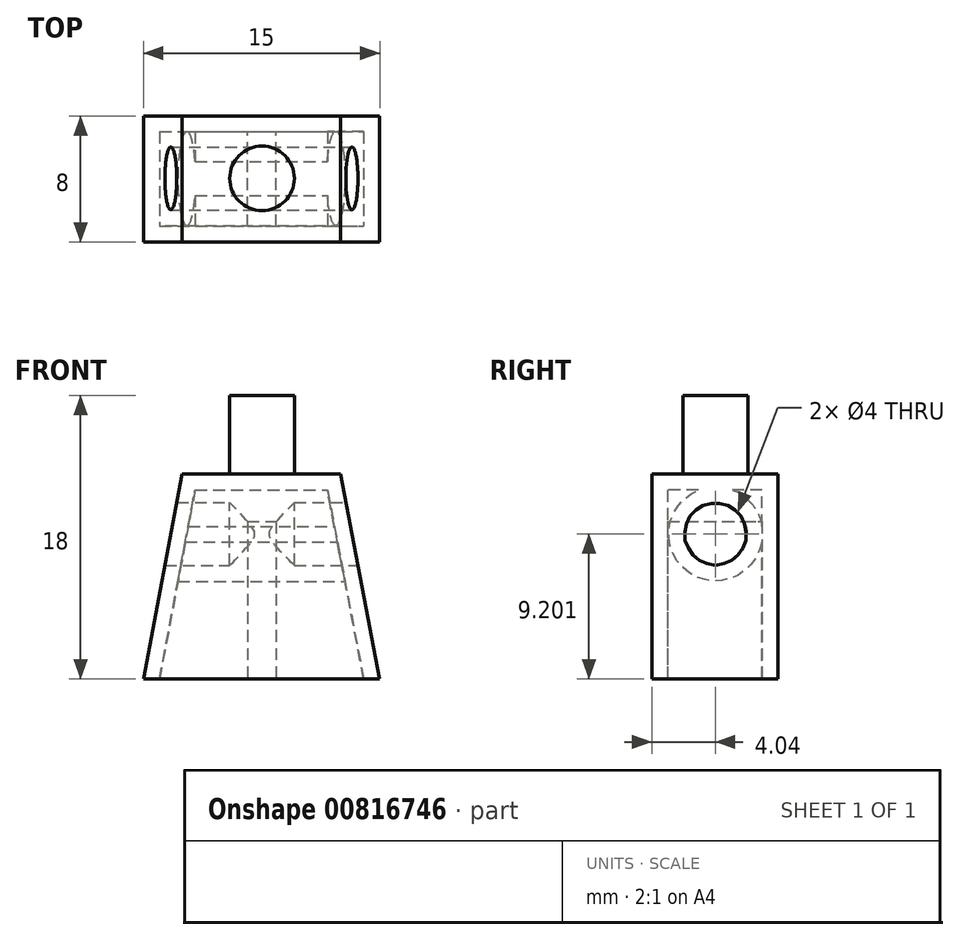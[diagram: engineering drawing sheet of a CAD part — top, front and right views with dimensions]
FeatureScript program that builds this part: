
annotation { "Feature Type Name" : "Feature", "Feature Type Description" : "" }
export const myFeature = defineFeature(function(context is Context, id is Id, definition is map)
    precondition{}
    {
        {
            var Q0;
            Q0=qCreatedBy(makeId("Top.planeOp"),FACE);
            var sketch = newSketch(context, id + "F0", { "sketchPlane" : qUnion([Q0])});
            skLineSegment(sketch, "E0.bottom", {"start": v(-7.52, 3.96) * mm, "end": v(7.48, 3.96) * mm});
            skLineSegment(sketch, "E0.top", {"start": v(-7.52, -4.04) * mm, "end": v(7.48, -4.04) * mm});
            skLineSegment(sketch, "E0.left", {"start": v(-7.52, 3.96) * mm, "end": v(-7.52, -4.04) * mm});
            skLineSegment(sketch, "E0.right", {"start": v(7.48, 3.96) * mm, "end": v(7.48, -4.04) * mm});
            skSolve(sketch);
        }
        {
            var Q0;
            Q0 = qSketchRegion(id + "F0", true);
            extrude(context, id + "F1", {"entities" : qUnion([Q0]), "depth" : 13 * mm, "offsetDistance" : 25 * mm});
        }
        {
            var Q0;
            Q0=makeQuery(id+"F1.opExtrude","CAP_FACE",FACE,{"disambiguationData":[OSD([sQuery(id+"F0.wireOp",EDGE,"E0.bottom"),sQuery(id+"F0.wireOp",EDGE,"E0.top"),sQuery(id+"F0.wireOp",EDGE,"E0.left"),sQuery(id+"F0.wireOp",EDGE,"E0.right")])],"isStart":false});
            var sketch = newSketch(context, id + "F2", { "sketchPlane" : qUnion([Q0])});
            skLineSegment(sketch, "E1.bottom", {"start": v(-5.04, 3.96) * mm, "end": v(4.96, 3.96) * mm});
            skLineSegment(sketch, "E1.top", {"start": v(-5.04, -4.04) * mm, "end": v(4.96, -4.04) * mm});
            skLineSegment(sketch, "E1.left", {"start": v(-5.04, 3.96) * mm, "end": v(-5.04, -4.04) * mm});
            skLineSegment(sketch, "E1.right", {"start": v(4.96, 3.96) * mm, "end": v(4.96, -4.04) * mm});
            skSolve(sketch);
        }
        {
            var Q0;
            Q0=makeQuery(id+"F1.opExtrude","SWEPT_FACE",FACE,{"disambiguationData":[OSD([sQuery(id+"F0.wireOp",EDGE,"E0.top")])]});
            var sketch = newSketch(context, id + "F3", { "sketchPlane" : qUnion([Q0])});
            skLineSegment(sketch, "E2", {"start": v(-5.08, 13) * mm, "end": v(-7.52, 0) * mm});
            skLineSegment(sketch, "E3", {"start": v(-7.52, 0) * mm, "end": v(-7.52, 13) * mm});
            skLineSegment(sketch, "E4", {"start": v(-7.52, 13) * mm, "end": v(-5.08, 13) * mm});
            skLineSegment(sketch, "E5", {"start": v(4.98, 13) * mm, "end": v(7.48, 0) * mm});
            skLineSegment(sketch, "E6", {"start": v(7.48, 0) * mm, "end": v(7.48, 13) * mm});
            skLineSegment(sketch, "E7", {"start": v(7.48, 13) * mm, "end": v(4.98, 13) * mm});
            skSolve(sketch);
        }
        {
            var Q0;
            Q0 = qSketchRegion(id + "F3", true);
            extrude(context, id + "F4", {"entities" : qUnion([Q0]), "operationType" : NewBodyOperationType.REMOVE, "oppositeDirection" : true, "depth" : 25 * mm, "offsetDistance" : 25 * mm});
        }
        {
            var Q0;
            Q0=makeQuery(id+"F2.imprint","IMPRINT",FACE,{"disambiguationData":[TD([[makeQuery(id+"F2.imprint","IMPRINT",EDGE,{"derivedFrom":sQuery(id+"F2.wireOp",EDGE,"E1.bottom")}),-1.0]])]});
            var sketch = newSketch(context, id + "F5", { "sketchPlane" : qUnion([Q0])});
            skCircle(sketch, "E8", {"center": v(0, 0) * mm, "radius": 2.05 * mm});
            skSolve(sketch);
        }
        {
            var Q0;
            Q0 = qSketchRegion(id + "F5", true);
            extrude(context, id + "F6", {"entities" : qUnion([Q0]), "operationType" : NewBodyOperationType.ADD, "depth" : 5 * mm, "offsetDistance" : 25 * mm});
        }
        {
            var Q0;
            Q0=qCreatedBy(makeId("Right.planeOp"),FACE);
            var sketch = newSketch(context, id + "F7", { "sketchPlane" : qUnion([Q0])});
            skCircle(sketch, "E9", {"center": v(0, 9.2) * mm, "radius": 2 * mm});
            skSolve(sketch);
        }
        {
            var Q0;
            Q0 = qSketchRegion(id + "F7", true);
            extrude(context, id + "F8", {"entities" : qUnion([Q0]), "operationType" : NewBodyOperationType.REMOVE, "oppositeDirection" : true, "depth" : 25 * mm, "offsetDistance" : 25 * mm, "hasSecondDirection" : true, "secondDirectionOppositeDirection" : false, "secondDirectionDepth" : 25 * mm});
        }
        {
            var Q0;
            Q0=makeQuery(id+"F6.opExtrude","CAP_FACE",FACE,{"disambiguationData":[OSD([sQuery(id+"F5.wireOp",EDGE,"E8")])],"isStart":false});
            extrude(context, id + "F9", {"entities" : qUnion([Q0]), "operationType" : NewBodyOperationType.ADD, "oppositeDirection" : true, "depth" : 13 * mm, "offsetDistance" : 25 * mm});
        }
        {
            var Q0;
            Q0=makeQuery(id+"F1.opExtrude","CAP_FACE",FACE,{"disambiguationData":[OSD([sQuery(id+"F0.wireOp",EDGE,"E0.bottom"),sQuery(id+"F0.wireOp",EDGE,"E0.top"),sQuery(id+"F0.wireOp",EDGE,"E0.left"),sQuery(id+"F0.wireOp",EDGE,"E0.right")])],"isStart":true});
            shell(context, id + "F10", {"entities" : qUnion([Q0]), "thickness" : 1 * mm});
        }
        {
            var Q0;
            Q0=makeQuery(id+"F1.opExtrude","CAP_FACE",FACE,{"disambiguationData":[OSD([sQuery(id+"F0.wireOp",EDGE,"E0.bottom"),sQuery(id+"F0.wireOp",EDGE,"E0.top"),sQuery(id+"F0.wireOp",EDGE,"E0.left"),sQuery(id+"F0.wireOp",EDGE,"E0.right")])],"isStart":true});
            var sketch = newSketch(context, id + "F11", { "sketchPlane" : qUnion([Q0])});
            skLineSegment(sketch, "E10.bottom", {"start": v(-0.92, 4.04) * mm, "end": v(0.88, 4.04) * mm});
            skLineSegment(sketch, "E10.top", {"start": v(-0.92, -3.96) * mm, "end": v(0.88, -3.96) * mm});
            skLineSegment(sketch, "E10.left", {"start": v(-0.92, 4.04) * mm, "end": v(-0.92, -3.96) * mm});
            skLineSegment(sketch, "E10.right", {"start": v(0.88, 4.04) * mm, "end": v(0.88, -3.96) * mm});
            skSolve(sketch);
        }
        {
            var Q0;
            {var subQ0=sQuery(id+"F11.wireOp",EDGE,"E10.left");var subQ1=sQuery(id+"F0.wireOp",EDGE,"E0.top");var subQ2=makeQuery(id+"F10.opShell","OFFSET_EDGE",EDGE,{"disambiguationData":[OSD([subQ1]),TDD([makeQuery(id+"F1.opExtrude","CAP_EDGE",EDGE,{"disambiguationData":[OSD([subQ1])],"isStart":true})])]});var subQ3=makeQuery(id+"F11.imprint","INTERSECT",VERTEX,{"derivedFrom":[subQ2,subQ0]});Q0=makeQuery(id+"F11.imprint","IMPRINT",FACE,{"disambiguationData":[TD([[makeQuery(id+"F11.imprint","IMPRINT",EDGE,{"disambiguationData":[TD([[subQ3,-1.0]])],"derivedFrom":subQ0}),1.0]])]});}
            extrude(context, id + "F12", {"entities" : qUnion([Q0]), "oppositeDirection" : true, "depth" : 10 * mm, "offsetDistance" : 25 * mm});
        }
    });
